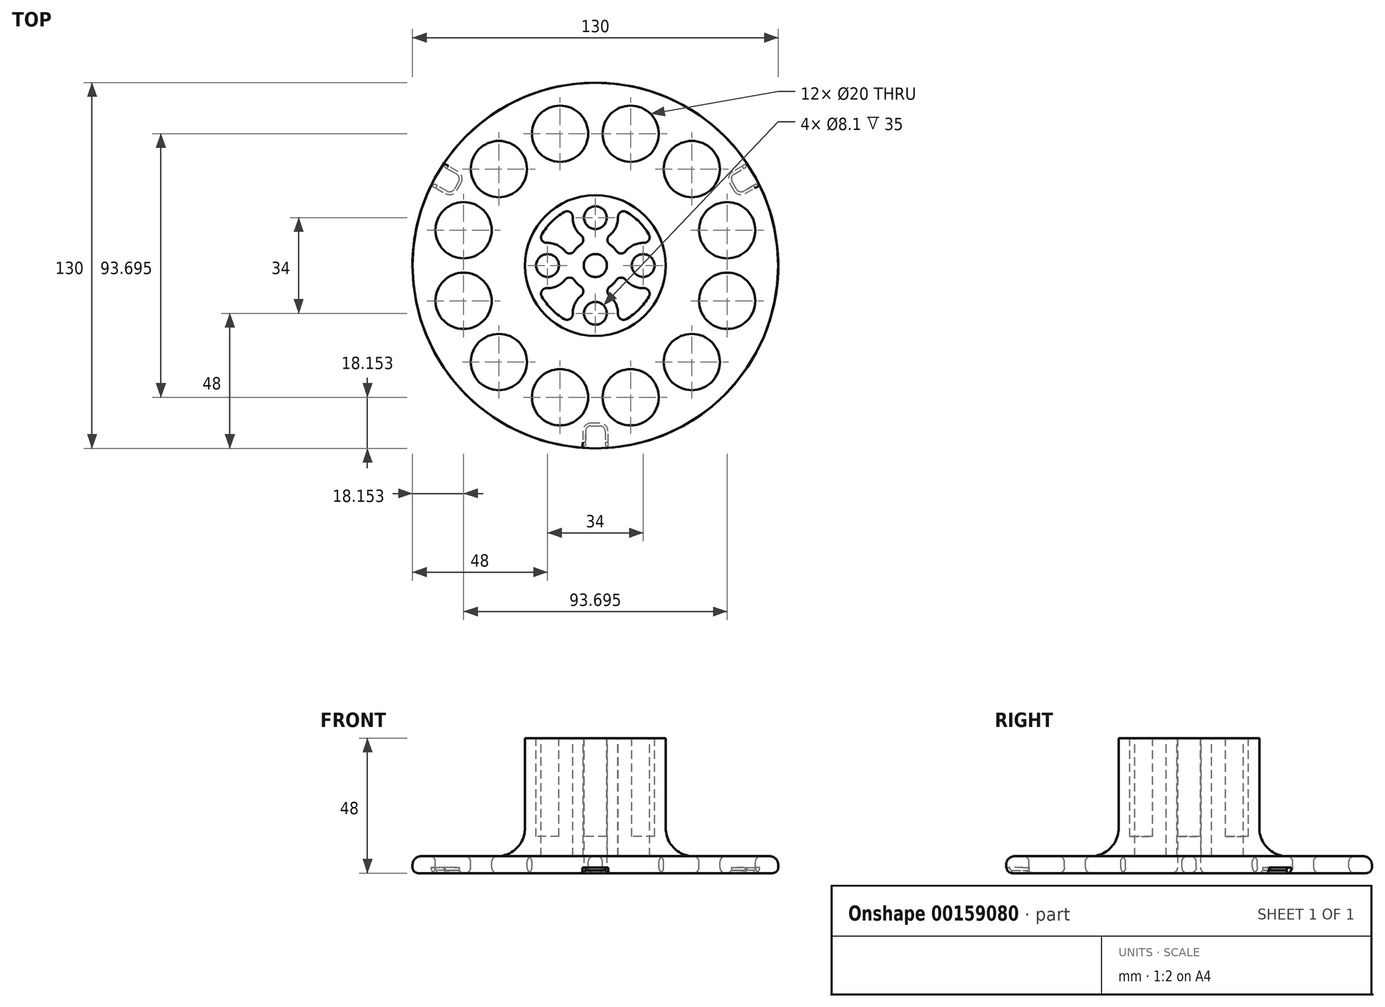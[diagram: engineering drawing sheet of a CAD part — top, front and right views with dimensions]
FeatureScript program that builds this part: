
annotation { "Feature Type Name" : "Feature", "Feature Type Description" : "" }
export const myFeature = defineFeature(function(context is Context, id is Id, definition is map)
    precondition{}
    {
        {
            var Q0;
            Q0=qCreatedBy(makeId("Right.planeOp"),FACE);
            var sketch = newSketch(context, id + "F0", { "sketchPlane" : qUnion([Q0])});
            skLineSegment(sketch, "E0", {"start": v(4.1, 48) * mm, "end": v(4.1, 2) * mm});
            skLineSegment(sketch, "E1", {"start": v(6.1, 0) * mm, "end": v(63, 0) * mm});
            skLineSegment(sketch, "E2", {"start": v(65, 2) * mm, "end": v(65, 3) * mm});
            skLineSegment(sketch, "E3", {"start": v(62, 6) * mm, "end": v(35, 6) * mm});
            skLineSegment(sketch, "E4", {"start": v(25, 16) * mm, "end": v(25, 48) * mm});
            skLineSegment(sketch, "E5", {"start": v(25, 48) * mm, "end": v(4.1, 48) * mm});
            skPoint(sketch, "E6.visualSharp", {"position": v(25, 6) * mm});
            skArc(sketch, "E6.filletArc", {"start": v(25, 16) * mm, "mid": v(27.93, 8.93) * mm, "end": v(35, 6) * mm});
            skPoint(sketch, "E7.visualSharp", {"position": v(4.1, 0) * mm});
            skArc(sketch, "E7.filletArc", {"start": v(4.1, 2) * mm, "mid": v(4.69, 0.59) * mm, "end": v(6.1, 0) * mm});
            skPoint(sketch, "E8.visualSharp", {"position": v(65, 6) * mm});
            skPoint(sketch, "E9.visualSharp", {"position": v(65, 0) * mm});
            skArc(sketch, "E9.filletArc", {"start": v(63, 0) * mm, "mid": v(64.41, 0.59) * mm, "end": v(65, 2) * mm});
            skLineSegment(sketch, "E10", {"start": v(0, 0) * mm, "end": v(0, 48) * mm, "construction": true});
            skArc(sketch, "E11.filletArc", {"start": v(65, 3) * mm, "mid": v(64.12, 5.12) * mm, "end": v(62, 6) * mm});
            skSolve(sketch);
        }
        {
            var Q0;
            Q0 = qSketchRegion(id + "F0", true);
            var Q1;
            Q1=sQuery(id+"F0.wireOp",EDGE,"E10");
            revolve(context, id + "F1", {"entities" : qUnion([Q0]), "axis" : qUnion([Q1]), "revolveType" : RevolveType.FULL});
        }
        {
            var Q0;
            Q0=makeQuery(id+"F1.opRevolve","SWEPT_FACE",FACE,{"disambiguationData":[OSD([sQuery(id+"F0.wireOp",EDGE,"E3")])]});
            var sketch = newSketch(context, id + "F2", { "sketchPlane" : qUnion([Q0])});
            skCircle(sketch, "E12", {"center": v(-46.85, -12.55) * mm, "radius": 10 * mm});
            skCircle(sketch, "E13.1.0", {"center": v(-34.3, -34.3) * mm, "radius": 10 * mm});
            skCircle(sketch, "E13.2.0", {"center": v(-12.55, -46.85) * mm, "radius": 10 * mm});
            skCircle(sketch, "E13.3.0", {"center": v(12.55, -46.85) * mm, "radius": 10 * mm});
            skCircle(sketch, "E13.4.0", {"center": v(34.3, -34.3) * mm, "radius": 10 * mm});
            skCircle(sketch, "E13.5.0", {"center": v(46.85, -12.55) * mm, "radius": 10 * mm});
            skCircle(sketch, "E13.6.0", {"center": v(46.85, 12.55) * mm, "radius": 10 * mm});
            skCircle(sketch, "E13.7.0", {"center": v(34.3, 34.3) * mm, "radius": 10 * mm});
            skPoint(sketch, "E13.center", {"position": v(0, 0) * mm});
            skCircle(sketch, "E14.1.8.0", {"center": v(12.55, 46.85) * mm, "radius": 10 * mm});
            skCircle(sketch, "E15.1.9.0", {"center": v(-12.55, 46.85) * mm, "radius": 10 * mm});
            skCircle(sketch, "E15.1.10.0", {"center": v(-34.3, 34.3) * mm, "radius": 10 * mm});
            skCircle(sketch, "E15.1.11.0", {"center": v(-46.85, 12.55) * mm, "radius": 10 * mm});
            skLineSegment(sketch, "E16", {"start": v(0, 0) * mm, "end": v(-73.77, -19.77) * mm, "construction": true});
            skSolve(sketch);
        }
        {
            var Q0;
            Q0 = qSketchRegion(id + "F2", true);
            extrude(context, id + "F3", {"entities" : qUnion([Q0]), "operationType" : NewBodyOperationType.REMOVE, "endBound" : BoundingType.THROUGH_ALL, "oppositeDirection" : true, "depth" : 25 * mm});
        }
        {
            var Q0;
            Q0=makeQuery(id+"F1.opRevolve","SWEPT_FACE",FACE,{"disambiguationData":[OSD([sQuery(id+"F0.wireOp",EDGE,"E5")])]});
            var sketch = newSketch(context, id + "F4", { "sketchPlane" : qUnion([Q0])});
            skCircle(sketch, "E17", {"center": v(0, -17) * mm, "radius": 4.05 * mm});
            skCircle(sketch, "E18.1.0", {"center": v(17, 0) * mm, "radius": 4.05 * mm});
            skCircle(sketch, "E18.2.0", {"center": v(0, 17) * mm, "radius": 4.05 * mm});
            skCircle(sketch, "E18.3.0", {"center": v(-17, 0) * mm, "radius": 4.05 * mm});
            skPoint(sketch, "E18.center", {"position": v(0, 0) * mm});
            skSolve(sketch);
        }
        {
            var Q0;
            Q0 = qSketchRegion(id + "F4", true);
            extrude(context, id + "F5", {"entities" : qUnion([Q0]), "operationType" : NewBodyOperationType.REMOVE, "oppositeDirection" : true, "depth" : 35 * mm});
        }
        {
            var Q0;
            Q0=makeQuery(id+"F1.opRevolve","SWEPT_FACE",FACE,{"disambiguationData":[OSD([sQuery(id+"F0.wireOp",EDGE,"E5")])]});
            var sketch = newSketch(context, id + "F6", { "sketchPlane" : qUnion([Q0])});
            skArc(sketch, "E19.0", {"start": v(-8.05, 17.24) * mm, "mid": v(-7.3, 13.62) * mm, "end": v(-5.03, 10.71) * mm});
            skArc(sketch, "E20.0", {"start": v(17.24, 8.05) * mm, "mid": v(13.62, 7.3) * mm, "end": v(10.71, 5.03) * mm});
            skArc(sketch, "E21.0", {"start": v(8.05, -17.24) * mm, "mid": v(7.3, -13.62) * mm, "end": v(5.03, -10.71) * mm});
            skArc(sketch, "E22.0", {"start": v(-17.24, -8.05) * mm, "mid": v(-13.62, -7.3) * mm, "end": v(-10.71, -5.03) * mm});
            skArc(sketch, "E23.0", {"start": v(-5.15, 7.5) * mm, "mid": v(-6.43, 6.43) * mm, "end": v(-7.5, 5.15) * mm});
            skArc(sketch, "E24.0", {"start": v(11.05, -19.02) * mm, "mid": v(15.56, -15.56) * mm, "end": v(19.02, -11.05) * mm});
            skArc(sketch, "E25.trimOffspring", {"start": v(19.02, 11.05) * mm, "mid": v(15.56, 15.56) * mm, "end": v(11.05, 19.02) * mm});
            skArc(sketch, "E26.trimOffspring", {"start": v(-19.02, -11.05) * mm, "mid": v(-15.56, -15.56) * mm, "end": v(-11.05, -19.02) * mm});
            skArc(sketch, "E27.trimOffspring", {"start": v(-11.05, 19.02) * mm, "mid": v(-15.56, 15.56) * mm, "end": v(-19.02, 11.05) * mm});
            skArc(sketch, "E28.trimOffspring", {"start": v(5.03, 10.71) * mm, "mid": v(7.3, 13.62) * mm, "end": v(8.05, 17.24) * mm});
            skArc(sketch, "E29.trimOffspring", {"start": v(10.71, -5.03) * mm, "mid": v(13.62, -7.3) * mm, "end": v(17.24, -8.05) * mm});
            skArc(sketch, "E30.trimOffspring", {"start": v(7.5, 5.15) * mm, "mid": v(6.43, 6.43) * mm, "end": v(5.15, 7.5) * mm});
            skArc(sketch, "E31.trimOffspring", {"start": v(-10.71, 5.03) * mm, "mid": v(-13.62, 7.3) * mm, "end": v(-17.24, 8.05) * mm});
            skArc(sketch, "E32.trimOffspring", {"start": v(-7.5, -5.15) * mm, "mid": v(-6.43, -6.43) * mm, "end": v(-5.15, -7.5) * mm});
            skArc(sketch, "E33.trimOffspring", {"start": v(-5.03, -10.71) * mm, "mid": v(-7.3, -13.62) * mm, "end": v(-8.05, -17.24) * mm});
            skArc(sketch, "E34.trimOffspring", {"start": v(5.15, -7.5) * mm, "mid": v(6.43, -6.43) * mm, "end": v(7.5, -5.15) * mm});
            skPoint(sketch, "E35.visualSharp", {"position": v(-9.03, -1.13) * mm});
            skArc(sketch, "E35.filletArc", {"start": v(-7.5, -5.15) * mm, "mid": v(-9.08, -4.28) * mm, "end": v(-10.71, -5.03) * mm});
            skPoint(sketch, "E36.visualSharp", {"position": v(-9.03, 1.13) * mm});
            skArc(sketch, "E36.filletArc", {"start": v(-10.71, 5.03) * mm, "mid": v(-9.08, 4.28) * mm, "end": v(-7.5, 5.15) * mm});
            skPoint(sketch, "E37.visualSharp", {"position": v(-20.83, -7.08) * mm});
            skArc(sketch, "E37.filletArc", {"start": v(-17.24, -8.05) * mm, "mid": v(-19.01, -9.02) * mm, "end": v(-19.02, -11.05) * mm});
            skPoint(sketch, "E38.visualSharp", {"position": v(-20.83, 7.08) * mm});
            skArc(sketch, "E38.filletArc", {"start": v(-19.02, 11.05) * mm, "mid": v(-19.01, 9.02) * mm, "end": v(-17.24, 8.05) * mm});
            skPoint(sketch, "E39.visualSharp", {"position": v(-1.13, 9.03) * mm});
            skArc(sketch, "E39.filletArc", {"start": v(-5.15, 7.5) * mm, "mid": v(-4.28, 9.08) * mm, "end": v(-5.03, 10.71) * mm});
            skPoint(sketch, "E40.visualSharp", {"position": v(1.13, 9.03) * mm});
            skArc(sketch, "E40.filletArc", {"start": v(5.03, 10.71) * mm, "mid": v(4.28, 9.08) * mm, "end": v(5.15, 7.5) * mm});
            skPoint(sketch, "E41.visualSharp", {"position": v(9.03, 1.13) * mm});
            skArc(sketch, "E41.filletArc", {"start": v(7.5, 5.15) * mm, "mid": v(9.08, 4.28) * mm, "end": v(10.71, 5.03) * mm});
            skPoint(sketch, "E42.visualSharp", {"position": v(9.03, -1.13) * mm});
            skArc(sketch, "E42.filletArc", {"start": v(10.71, -5.03) * mm, "mid": v(9.08, -4.28) * mm, "end": v(7.5, -5.15) * mm});
            skPoint(sketch, "E43.visualSharp", {"position": v(1.13, -9.03) * mm});
            skArc(sketch, "E43.filletArc", {"start": v(5.15, -7.5) * mm, "mid": v(4.28, -9.08) * mm, "end": v(5.03, -10.71) * mm});
            skPoint(sketch, "E44.visualSharp", {"position": v(-1.13, -9.03) * mm});
            skArc(sketch, "E44.filletArc", {"start": v(-5.03, -10.71) * mm, "mid": v(-4.28, -9.08) * mm, "end": v(-5.15, -7.5) * mm});
            skPoint(sketch, "E45.visualSharp", {"position": v(20.83, -7.08) * mm});
            skArc(sketch, "E45.filletArc", {"start": v(19.02, -11.05) * mm, "mid": v(19.01, -9.02) * mm, "end": v(17.24, -8.05) * mm});
            skPoint(sketch, "E46.visualSharp", {"position": v(7.08, -20.83) * mm});
            skArc(sketch, "E46.filletArc", {"start": v(8.05, -17.24) * mm, "mid": v(9.02, -19.01) * mm, "end": v(11.05, -19.02) * mm});
            skPoint(sketch, "E47.visualSharp", {"position": v(-7.08, -20.83) * mm});
            skArc(sketch, "E47.filletArc", {"start": v(-11.05, -19.02) * mm, "mid": v(-9.02, -19.01) * mm, "end": v(-8.05, -17.24) * mm});
            skPoint(sketch, "E48.visualSharp", {"position": v(20.83, 7.08) * mm});
            skArc(sketch, "E48.filletArc", {"start": v(17.24, 8.05) * mm, "mid": v(19.01, 9.02) * mm, "end": v(19.02, 11.05) * mm});
            skPoint(sketch, "E49.visualSharp", {"position": v(7.08, 20.83) * mm});
            skArc(sketch, "E49.filletArc", {"start": v(11.05, 19.02) * mm, "mid": v(9.02, 19.01) * mm, "end": v(8.05, 17.24) * mm});
            skPoint(sketch, "E50.visualSharp", {"position": v(-7.08, 20.83) * mm});
            skArc(sketch, "E50.filletArc", {"start": v(-8.05, 17.24) * mm, "mid": v(-9.02, 19.01) * mm, "end": v(-11.05, 19.02) * mm});
            skSolve(sketch);
        }
        {
            var Q0;
            Q0 = qSketchRegion(id + "F6", true);
            extrude(context, id + "F7", {"entities" : qUnion([Q0]), "operationType" : NewBodyOperationType.REMOVE, "oppositeDirection" : true, "depth" : 42 * mm});
        }
        {
            var Q0;
            Q0=makeQuery(id+"F1.opRevolve","SWEPT_FACE",FACE,{"disambiguationData":[OSD([sQuery(id+"F0.wireOp",EDGE,"E3")])]});
            var Q1;
            Q1=makeQuery(id+"F1.opRevolve","SWEPT_FACE",FACE,{"disambiguationData":[OSD([sQuery(id+"F0.wireOp",EDGE,"E1")])]});
            fillet(context, id + "F8", {"entities" : qUnion([Q0, Q1]), "radius" : 2 * mm, "tangentPropagation" : true, "allowEdgeOverflow" : false});
        }
        {
            var Q0;
            Q0=makeQuery(id+"F1.opRevolve","SWEPT_FACE",FACE,{"disambiguationData":[OSD([sQuery(id+"F0.wireOp",EDGE,"E1")])]});
            var sketch = newSketch(context, id + "F9", { "sketchPlane" : qUnion([Q0])});
            skLineSegment(sketch, "E51.bottom", {"start": v(1.5, 57) * mm, "end": v(-1.5, 57) * mm});
            skLineSegment(sketch, "E51.top", {"start": v(3.5, 69) * mm, "end": v(-3.5, 69) * mm});
            skLineSegment(sketch, "E51.left", {"start": v(3.5, 59) * mm, "end": v(3.5, 69) * mm});
            skLineSegment(sketch, "E51.right", {"start": v(-3.5, 59) * mm, "end": v(-3.5, 69) * mm});
            skPoint(sketch, "E51.middle", {"position": v(0, 63) * mm});
            skPoint(sketch, "E52.visualSharp", {"position": v(-3.5, 57) * mm});
            skArc(sketch, "E52.filletArc", {"start": v(-3.5, 59) * mm, "mid": v(-2.91, 57.59) * mm, "end": v(-1.5, 57) * mm});
            skPoint(sketch, "E53.visualSharp", {"position": v(3.5, 57) * mm});
            skArc(sketch, "E53.filletArc", {"start": v(1.5, 57) * mm, "mid": v(2.91, 57.59) * mm, "end": v(3.5, 59) * mm});
            skPoint(sketch, "E54.1.0", {"position": v(-54.56, -31.5) * mm});
            skLineSegment(sketch, "E54.1.1", {"start": v(-49.35, -32.53) * mm, "end": v(-58, -37.53) * mm});
            skPoint(sketch, "E54.1.2", {"position": v(-47.61, -31.53) * mm});
            skPoint(sketch, "E54.1.3", {"position": v(-51.11, -25.47) * mm});
            skLineSegment(sketch, "E54.1.4", {"start": v(-61.5, -31.47) * mm, "end": v(-58, -37.53) * mm});
            skLineSegment(sketch, "E54.1.5", {"start": v(-52.85, -26.47) * mm, "end": v(-61.5, -31.47) * mm});
            skArc(sketch, "E54.1.6", {"start": v(-50.11, -27.2) * mm, "mid": v(-51.33, -26.27) * mm, "end": v(-52.85, -26.47) * mm});
            skArc(sketch, "E54.1.7", {"start": v(-49.35, -32.53) * mm, "mid": v(-48.41, -31.32) * mm, "end": v(-48.61, -29.8) * mm});
            skLineSegment(sketch, "E54.1.8", {"start": v(-50.11, -27.2) * mm, "end": v(-48.61, -29.8) * mm});
            skPoint(sketch, "E54.2.0", {"position": v(54.56, -31.5) * mm});
            skLineSegment(sketch, "E54.2.1", {"start": v(52.85, -26.47) * mm, "end": v(61.5, -31.47) * mm});
            skPoint(sketch, "E54.2.2", {"position": v(51.11, -25.47) * mm});
            skPoint(sketch, "E54.2.3", {"position": v(47.61, -31.53) * mm});
            skLineSegment(sketch, "E54.2.4", {"start": v(58, -37.53) * mm, "end": v(61.5, -31.47) * mm});
            skLineSegment(sketch, "E54.2.5", {"start": v(49.35, -32.53) * mm, "end": v(58, -37.53) * mm});
            skArc(sketch, "E54.2.6", {"start": v(48.61, -29.8) * mm, "mid": v(48.41, -31.32) * mm, "end": v(49.35, -32.53) * mm});
            skArc(sketch, "E54.2.7", {"start": v(52.85, -26.47) * mm, "mid": v(51.33, -26.27) * mm, "end": v(50.11, -27.2) * mm});
            skLineSegment(sketch, "E54.2.8", {"start": v(48.61, -29.8) * mm, "end": v(50.11, -27.2) * mm});
            skPoint(sketch, "E54.center", {"position": v(0, 0) * mm});
            skSolve(sketch);
        }
        {
            var Q0;
            Q0 = qSketchRegion(id + "F9", true);
            extrude(context, id + "F10", {"entities" : qUnion([Q0]), "operationType" : NewBodyOperationType.REMOVE, "oppositeDirection" : true, "depth" : 2 * mm});
        }
        {
            var Q0;
            Q0=makeQuery(id+"F10.boolean.opBoolean","COPY",EDGE,{"derivedFrom":makeQuery(id+"F10.opExtrude","CAP_EDGE",EDGE,{"disambiguationData":[OSD([sQuery(id+"F9.wireOp",EDGE,"E51.right")])],"isStart":true})});
            var Q1;
            Q1=makeQuery(id+"F10.boolean.opBoolean","COPY",EDGE,{"derivedFrom":makeQuery(id+"F10.opExtrude","CAP_EDGE",EDGE,{"disambiguationData":[OSD([sQuery(id+"F9.wireOp",EDGE,"E52.filletArc")])],"isStart":true})});
            var Q2;
            Q2=makeQuery(id+"F10.boolean.opBoolean","COPY",EDGE,{"derivedFrom":makeQuery(id+"F10.opExtrude","CAP_EDGE",EDGE,{"disambiguationData":[OSD([sQuery(id+"F9.wireOp",EDGE,"E51.bottom")])],"isStart":true})});
            var Q3;
            Q3=makeQuery(id+"F10.boolean.opBoolean","COPY",EDGE,{"derivedFrom":makeQuery(id+"F10.opExtrude","CAP_EDGE",EDGE,{"disambiguationData":[OSD([sQuery(id+"F9.wireOp",EDGE,"E53.filletArc")])],"isStart":true})});
            var Q4;
            Q4=makeQuery(id+"F10.boolean.opBoolean","COPY",EDGE,{"derivedFrom":makeQuery(id+"F10.opExtrude","CAP_EDGE",EDGE,{"disambiguationData":[OSD([sQuery(id+"F9.wireOp",EDGE,"E51.left")])],"isStart":true})});
            var Q5;
            Q5=makeQuery(id+"F10.boolean.opBoolean","INTERSECT",EDGE,{"derivedFrom":[makeQuery(id+"F1.opRevolve","SWEPT_FACE",FACE,{"disambiguationData":[OSD([sQuery(id+"F0.wireOp",EDGE,"E9.filletArc")])]}),makeQuery(id+"F10.opExtrude","SWEPT_FACE",FACE,{"disambiguationData":[OSD([sQuery(id+"F9.wireOp",EDGE,"E51.left")])]})]});
            var Q6;
            Q6=makeQuery(id+"F10.boolean.opBoolean","INTERSECT",EDGE,{"derivedFrom":[makeQuery(id+"F1.opRevolve","SWEPT_FACE",FACE,{"disambiguationData":[OSD([sQuery(id+"F0.wireOp",EDGE,"E9.filletArc")])]}),makeQuery(id+"F10.opExtrude","SWEPT_FACE",FACE,{"disambiguationData":[OSD([sQuery(id+"F9.wireOp",EDGE,"E51.right")])]})]});
            var Q7;
            Q7=makeQuery(id+"F10.boolean.opBoolean","COPY",EDGE,{"derivedFrom":makeQuery(id+"F10.opExtrude","CAP_EDGE",EDGE,{"disambiguationData":[OSD([sQuery(id+"F9.wireOp",EDGE,"E54.1.1")])],"isStart":true})});
            var Q8;
            Q8=makeQuery(id+"F10.boolean.opBoolean","COPY",EDGE,{"derivedFrom":makeQuery(id+"F10.opExtrude","CAP_EDGE",EDGE,{"disambiguationData":[OSD([sQuery(id+"F9.wireOp",EDGE,"E54.1.7")])],"isStart":true})});
            var Q9;
            Q9=makeQuery(id+"F10.boolean.opBoolean","COPY",EDGE,{"derivedFrom":makeQuery(id+"F10.opExtrude","CAP_EDGE",EDGE,{"disambiguationData":[OSD([sQuery(id+"F9.wireOp",EDGE,"E54.1.8")])],"isStart":true})});
            var Q10;
            Q10=makeQuery(id+"F10.boolean.opBoolean","COPY",EDGE,{"derivedFrom":makeQuery(id+"F10.opExtrude","CAP_EDGE",EDGE,{"disambiguationData":[OSD([sQuery(id+"F9.wireOp",EDGE,"E54.1.6")])],"isStart":true})});
            var Q11;
            Q11=makeQuery(id+"F10.boolean.opBoolean","COPY",EDGE,{"derivedFrom":makeQuery(id+"F10.opExtrude","CAP_EDGE",EDGE,{"disambiguationData":[OSD([sQuery(id+"F9.wireOp",EDGE,"E54.1.5")])],"isStart":true})});
            var Q12;
            Q12=makeQuery(id+"F10.boolean.opBoolean","INTERSECT",EDGE,{"derivedFrom":[makeQuery(id+"F1.opRevolve","SWEPT_FACE",FACE,{"disambiguationData":[OSD([sQuery(id+"F0.wireOp",EDGE,"E9.filletArc")])]}),makeQuery(id+"F10.opExtrude","SWEPT_FACE",FACE,{"disambiguationData":[OSD([sQuery(id+"F9.wireOp",EDGE,"E54.1.5")])]})]});
            var Q13;
            Q13=makeQuery(id+"F10.boolean.opBoolean","INTERSECT",EDGE,{"derivedFrom":[makeQuery(id+"F1.opRevolve","SWEPT_FACE",FACE,{"disambiguationData":[OSD([sQuery(id+"F0.wireOp",EDGE,"E9.filletArc")])]}),makeQuery(id+"F10.opExtrude","SWEPT_FACE",FACE,{"disambiguationData":[OSD([sQuery(id+"F9.wireOp",EDGE,"E54.1.1")])]})]});
            var Q14;
            Q14=makeQuery(id+"F10.boolean.opBoolean","INTERSECT",EDGE,{"derivedFrom":[makeQuery(id+"F1.opRevolve","SWEPT_FACE",FACE,{"disambiguationData":[OSD([sQuery(id+"F0.wireOp",EDGE,"E9.filletArc")])]}),makeQuery(id+"F10.opExtrude","SWEPT_FACE",FACE,{"disambiguationData":[OSD([sQuery(id+"F9.wireOp",EDGE,"E54.2.1")])]})]});
            var Q15;
            Q15=makeQuery(id+"F10.boolean.opBoolean","COPY",EDGE,{"derivedFrom":makeQuery(id+"F10.opExtrude","CAP_EDGE",EDGE,{"disambiguationData":[OSD([sQuery(id+"F9.wireOp",EDGE,"E54.2.1")])],"isStart":true})});
            var Q16;
            Q16=makeQuery(id+"F10.boolean.opBoolean","COPY",EDGE,{"derivedFrom":makeQuery(id+"F10.opExtrude","CAP_EDGE",EDGE,{"disambiguationData":[OSD([sQuery(id+"F9.wireOp",EDGE,"E54.2.7")])],"isStart":true})});
            var Q17;
            Q17=makeQuery(id+"F10.boolean.opBoolean","COPY",EDGE,{"derivedFrom":makeQuery(id+"F10.opExtrude","CAP_EDGE",EDGE,{"disambiguationData":[OSD([sQuery(id+"F9.wireOp",EDGE,"E54.2.8")])],"isStart":true})});
            var Q18;
            Q18=makeQuery(id+"F10.boolean.opBoolean","COPY",EDGE,{"derivedFrom":makeQuery(id+"F10.opExtrude","CAP_EDGE",EDGE,{"disambiguationData":[OSD([sQuery(id+"F9.wireOp",EDGE,"E54.2.6")])],"isStart":true})});
            var Q19;
            Q19=makeQuery(id+"F10.boolean.opBoolean","COPY",EDGE,{"derivedFrom":makeQuery(id+"F10.opExtrude","CAP_EDGE",EDGE,{"disambiguationData":[OSD([sQuery(id+"F9.wireOp",EDGE,"E54.2.5")])],"isStart":true})});
            var Q20;
            Q20=makeQuery(id+"F10.boolean.opBoolean","INTERSECT",EDGE,{"derivedFrom":[makeQuery(id+"F1.opRevolve","SWEPT_FACE",FACE,{"disambiguationData":[OSD([sQuery(id+"F0.wireOp",EDGE,"E9.filletArc")])]}),makeQuery(id+"F10.opExtrude","SWEPT_FACE",FACE,{"disambiguationData":[OSD([sQuery(id+"F9.wireOp",EDGE,"E54.2.5")])]})]});
            chamfer(context, id + "F11", {"entities" : qUnion([Q0, Q1, Q2, Q3, Q4, Q5, Q6, Q7, Q8, Q9, Q10, Q11, Q12, Q13, Q14, Q15, Q16, Q17, Q18, Q19, Q20]), "width" : 1 * mm, "tangentPropagation" : true});
        }
    });
